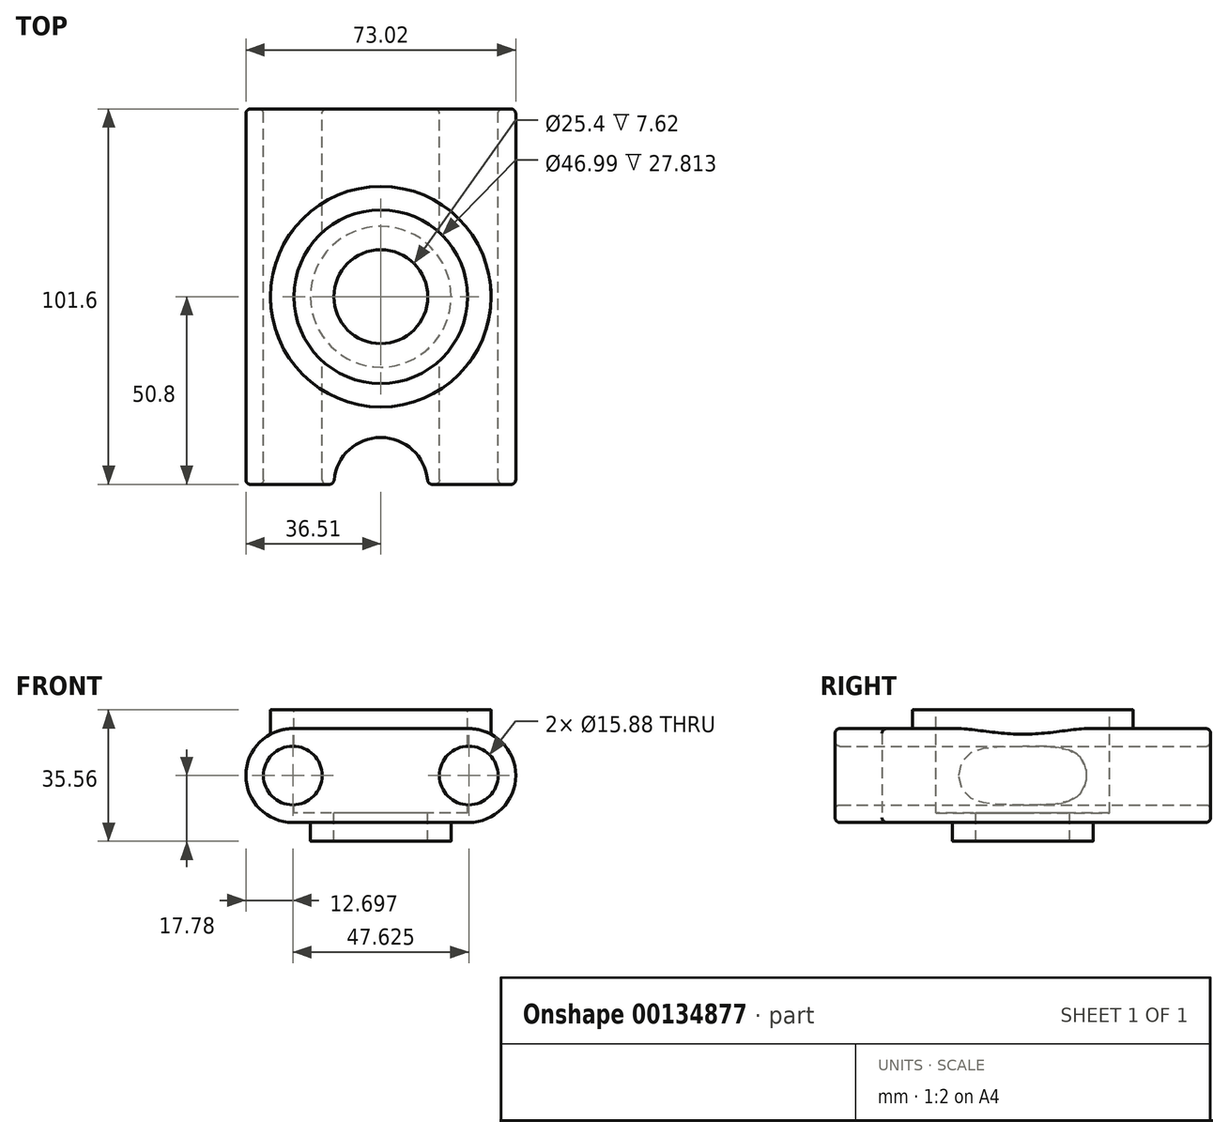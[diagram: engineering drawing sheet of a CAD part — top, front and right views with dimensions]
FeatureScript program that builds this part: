
annotation { "Feature Type Name" : "Feature", "Feature Type Description" : "" }
export const myFeature = defineFeature(function(context is Context, id is Id, definition is map)
    precondition{}
    {
        {
            var Q0;
            Q0=qCreatedBy(makeId("Front.planeOp"),FACE);
            var sketch = newSketch(context, id + "F0", { "sketchPlane" : qUnion([Q0])});
            skCircle(sketch, "E0", {"center": v(-23.81, 0) * mm, "radius": 7.94 * mm});
            skCircle(sketch, "E1", {"center": v(23.81, 0) * mm, "radius": 7.94 * mm});
            skLineSegment(sketch, "E2.bottom", {"start": v(-23.81, -12.7) * mm, "end": v(23.81, -12.7) * mm});
            skLineSegment(sketch, "E2.top", {"start": v(-23.81, 12.7) * mm, "end": v(23.81, 12.7) * mm});
            skLineSegment(sketch, "E3", {"start": v(0, 27.36) * mm, "end": v(0, -25.58) * mm});
            skArc(sketch, "E4.filletArc", {"start": v(-23.81, 12.7) * mm, "mid": v(-36.51, 0) * mm, "end": v(-23.81, -12.7) * mm});
            skLineSegment(sketch, "E5", {"start": v(41.42, 0) * mm, "end": v(-38.25, 0) * mm, "construction": true});
            skArc(sketch, "E6", {"start": v(23.81, -12.7) * mm, "mid": v(36.51, 0) * mm, "end": v(23.81, 12.7) * mm});
            skSolve(sketch);
        }
        {
            var Q0;
            {var subQ5=sQuery(id+"F0.wireOp",EDGE,"66a3805d-a401-4a56-aff0-8781810743c5.filletArc");Q0=makeQuery(id+"F0.imprint","IMPRINT",FACE,{"disambiguationData":[TD([[makeQuery(id+"F0.imprint","IMPRINT",EDGE,{"derivedFrom":subQ5}),1.0]])]});}
            var Q1;
            {var subQ0=sQuery(id+"F0.wireOp",EDGE,"bfb13ca5-58f2-4a11-b539-e9e0e547a674.filletArc");Q1=makeQuery(id+"F0.imprint","IMPRINT",FACE,{"disambiguationData":[TD([[makeQuery(id+"F0.imprint","IMPRINT",EDGE,{"derivedFrom":subQ0}),1.0]])]});}
            var Q2;
            {var subQ0=sQuery(id+"F0.wireOp",EDGE,"f594d6df-44da-47f5-ba40-ffa213aea947.filletArc");Q2=makeQuery(id+"F0.imprint","IMPRINT",FACE,{"disambiguationData":[TD([[makeQuery(id+"F0.imprint","IMPRINT",EDGE,{"derivedFrom":subQ0}),1.0]])]});}
            var Q3;
            {var subQ5=sQuery(id+"F0.wireOp",EDGE,"E4.filletArc");Q3=makeQuery(id+"F0.imprint","IMPRINT",FACE,{"disambiguationData":[TD([[makeQuery(id+"F0.imprint","IMPRINT",EDGE,{"derivedFrom":subQ5}),1.0]])]});}
            var Q4;
            Q4=makeQuery(id+"F0.imprint","IMPRINT",FACE,{"disambiguationData":[TD([[makeQuery(id+"F0.imprint","IMPRINT",EDGE,{"derivedFrom":sQuery(id+"F0.wireOp",EDGE,"E1")}),-1.0]])]});
            extrude(context, id + "F1", {"entities" : qUnion([Q0, Q1, Q2, Q3, Q4]), "depth" : 101.6 * mm, "symmetric" : true});
        }
        {
            var Q0;
            Q0=makeQuery(id+"F1.opExtrude","SWEPT_FACE",FACE,{"disambiguationData":[OSD([sQuery(id+"F0.wireOp",EDGE,"E2.top")])]});
            var sketch = newSketch(context, id + "F2", { "sketchPlane" : qUnion([Q0])});
            skCircle(sketch, "E7", {"center": v(0, 0) * mm, "radius": 12.7 * mm});
            skSolve(sketch);
        }
        {
            var Q0;
            Q0=makeQuery(id+"F2.imprint","IMPRINT",FACE,{"disambiguationData":[TD([[makeQuery(id+"F2.imprint","IMPRINT",EDGE,{"derivedFrom":sQuery(id+"F2.wireOp",EDGE,"E7")}),1.0]])]});
            extrude(context, id + "F3", {"entities" : qUnion([Q0]), "operationType" : NewBodyOperationType.REMOVE, "endBound" : BoundingType.THROUGH_ALL, "oppositeDirection" : true, "depth" : 25.4 * mm});
        }
        {
            var Q0;
            Q0=makeQuery(id+"F1.opExtrude","SWEPT_FACE",FACE,{"disambiguationData":[OSD([sQuery(id+"F0.wireOp",EDGE,"E2.top")])]});
            var sketch = newSketch(context, id + "F4", { "sketchPlane" : qUnion([Q0])});
            skCircle(sketch, "E8", {"center": v(0, 0) * mm, "radius": 23.5 * mm});
            skSolve(sketch);
        }
        {
            var Q0;
            Q0=makeQuery(id+"F4.imprint","IMPRINT",FACE,{"disambiguationData":[TD([[makeQuery(id+"F4.imprint","IMPRINT",EDGE,{"derivedFrom":sQuery(id+"F4.wireOp",EDGE,"E8")}),1.0]])]});
            extrude(context, id + "F5", {"entities" : qUnion([Q0]), "operationType" : NewBodyOperationType.REMOVE, "oppositeDirection" : true, "depth" : 22.86 * mm});
        }
        {
            var Q0;
            Q0=makeQuery(id+"F1.opExtrude","SWEPT_FACE",FACE,{"disambiguationData":[OSD([sQuery(id+"F0.wireOp",EDGE,"E2.bottom")])]});
            var sketch = newSketch(context, id + "F6", { "sketchPlane" : qUnion([Q0])});
            skCircle(sketch, "E9", {"center": v(0, 0) * mm, "radius": 19.05 * mm});
            skCircle(sketch, "E10", {"center": v(0, 0) * mm, "radius": 12.7 * mm});
            skSolve(sketch);
        }
        {
            var Q0;
            Q0=makeQuery(id+"F6.imprint","IMPRINT",FACE,{"disambiguationData":[TD([[makeQuery(id+"F6.imprint","IMPRINT",EDGE,{"derivedFrom":sQuery(id+"F6.wireOp",EDGE,"E9")}),1.0]])]});
            extrude(context, id + "F7", {"entities" : qUnion([Q0]), "operationType" : NewBodyOperationType.ADD, "depth" : 5.08 * mm});
        }
        {
            var Q0;
            Q0=makeQuery(id+"F1.opExtrude","SWEPT_FACE",FACE,{"disambiguationData":[OSD([sQuery(id+"F0.wireOp",EDGE,"E2.bottom")])]});
            var sketch = newSketch(context, id + "F8", { "sketchPlane" : qUnion([Q0])});
            skArc(sketch, "E11", {"start": v(-12.7, 50.8) * mm, "mid": v(0, 38.1) * mm, "end": v(12.7, 50.8) * mm});
            skLineSegment(sketch, "E12", {"start": v(-12.7, 50.8) * mm, "end": v(12.7, 50.8) * mm});
            skSolve(sketch);
        }
        {
            var Q0;
            Q0=makeQuery(id+"F8.imprint","IMPRINT",FACE,{"disambiguationData":[TD([[makeQuery(id+"F8.imprint","IMPRINT",EDGE,{"derivedFrom":sQuery(id+"F8.wireOp",EDGE,"E11")}),1.0]])]});
            extrude(context, id + "F9", {"entities" : qUnion([Q0]), "operationType" : NewBodyOperationType.REMOVE, "endBound" : BoundingType.THROUGH_ALL, "oppositeDirection" : true, "depth" : 25.4 * mm});
        }
        {
            var Q0;
            Q0=makeQuery(id+"F1.opExtrude","CAP_EDGE",EDGE,{"disambiguationData":[OSD([sQuery(id+"F0.wireOp",EDGE,"E2.top")])],"isStart":true});
            var Q1;
            {var subQ0=sQuery(id+"F0.wireOp",EDGE,"E4.filletArc");var subQ1=sQuery(id+"F0.wireOp",EDGE,"E2.bottom");var subQ2=sQuery(id+"F0.wireOp",EDGE,"E2.top");var subQ3=sQuery(id+"F0.wireOp",EDGE,"E0");Q1=makeQuery(id+"F9.boolean.opBoolean","SPLIT",FACE,{"disambiguationData":[TD([makeQuery(id+"F1.opExtrude","SWEPT_FACE",FACE,{"disambiguationData":[OSD([subQ3])]})])],"derivedFrom":makeQuery(id+"F1.opExtrude","CAP_FACE",FACE,{"disambiguationData":[OSD([subQ3,sQuery(id+"F0.wireOp",EDGE,"E1"),subQ1,subQ2,subQ0,sQuery(id+"F0.wireOp",EDGE,"E6")])],"isStart":false})});}
            var Q2;
            {var subQ0=sQuery(id+"F0.wireOp",EDGE,"E6");var subQ1=sQuery(id+"F0.wireOp",EDGE,"E2.top");var subQ2=sQuery(id+"F0.wireOp",EDGE,"E2.bottom");var subQ3=sQuery(id+"F0.wireOp",EDGE,"E1");Q2=makeQuery(id+"F9.boolean.opBoolean","SPLIT",FACE,{"disambiguationData":[TD([makeQuery(id+"F1.opExtrude","SWEPT_FACE",FACE,{"disambiguationData":[OSD([subQ3])]})])],"derivedFrom":makeQuery(id+"F1.opExtrude","CAP_FACE",FACE,{"disambiguationData":[OSD([sQuery(id+"F0.wireOp",EDGE,"E0"),subQ3,subQ2,subQ1,sQuery(id+"F0.wireOp",EDGE,"E4.filletArc"),subQ0])],"isStart":false})});}
            var Q3;
            Q3=makeQuery(id+"F9.boolean.opBoolean","COPY",FACE,{"derivedFrom":makeQuery(id+"F9.opExtrude","SWEPT_FACE",FACE,{"disambiguationData":[OSD([sQuery(id+"F8.wireOp",EDGE,"E11")])]})});
            var Q4;
            Q4=makeQuery(id+"F1.opExtrude","CAP_EDGE",EDGE,{"disambiguationData":[OSD([sQuery(id+"F0.wireOp",EDGE,"E1")])],"isStart":true});
            var Q5;
            Q5=makeQuery(id+"F1.opExtrude","CAP_EDGE",EDGE,{"disambiguationData":[OSD([sQuery(id+"F0.wireOp",EDGE,"E0")])],"isStart":true});
            fillet(context, id + "F10", {"entities" : qUnion([Q0, Q1, Q2, Q3, Q4, Q5]), "radius" : 1.27 * mm, "tangentPropagation" : true, "allowEdgeOverflow" : false});
        }
        {
            var Q0;
            Q0=makeQuery(id+"F1.opExtrude","SWEPT_FACE",FACE,{"disambiguationData":[OSD([sQuery(id+"F0.wireOp",EDGE,"E2.top")])]});
            cPlane(context, id + "F11", {"entities" : qUnion([Q0]), "cplaneType" : CPlaneType.OFFSET, "offset" : 5.08 * mm, "width" : 152.4 * mm, "height" : 152.4 * mm});
        }
        {
            var Q0;
            Q0=qCreatedBy(id+"F11.planeOp",FACE);
            var sketch = newSketch(context, id + "F12", { "sketchPlane" : qUnion([Q0])});
            skCircle(sketch, "E13", {"center": v(0, 0) * mm, "radius": 23.5 * mm});
            skCircle(sketch, "E14", {"center": v(0, 0) * mm, "radius": 29.85 * mm});
            skSolve(sketch);
        }
        {
            var Q0;
            Q0=makeQuery(id+"F12.imprint","IMPRINT",FACE,{"disambiguationData":[TD([[makeQuery(id+"F12.imprint","IMPRINT",EDGE,{"derivedFrom":sQuery(id+"F12.wireOp",EDGE,"E13")}),-1.0]])]});
            var Q1;
            Q1=makeQuery(id+"F1.opExtrude","SWEPT_FACE",FACE,{"disambiguationData":[OSD([sQuery(id+"F0.wireOp",EDGE,"E2.top")])]});
            extrude(context, id + "F13", {"entities" : qUnion([Q0]), "operationType" : NewBodyOperationType.ADD, "endBound" : BoundingType.UP_TO_NEXT, "oppositeDirection" : true, "endBoundEntityFace" : qUnion([Q1]), "depth" : 25.4 * mm});
        }
        {
            var Q0;
            Q0=makeQuery(id+"F13.opExtrude","CAP_EDGE",EDGE,{"disambiguationData":[OSD([sQuery(id+"F12.wireOp",EDGE,"E14")])],"isStart":true});
            var Q1;
            Q1=makeQuery(id+"F13.opExtrude","CAP_EDGE",EDGE,{"disambiguationData":[OSD([sQuery(id+"F12.wireOp",EDGE,"E13")])],"isStart":true});
            var Q2;
            Q2=makeQuery(id+"F7.opExtrude","CAP_EDGE",EDGE,{"disambiguationData":[OSD([sQuery(id+"F6.wireOp",EDGE,"E9")])],"isStart":false});
            fillet(context, id + "F14", {"entities" : qUnion([Q0, Q1, Q2]), "radius" : 0.13 * mm, "tangentPropagation" : true, "allowEdgeOverflow" : false});
        }
    });
